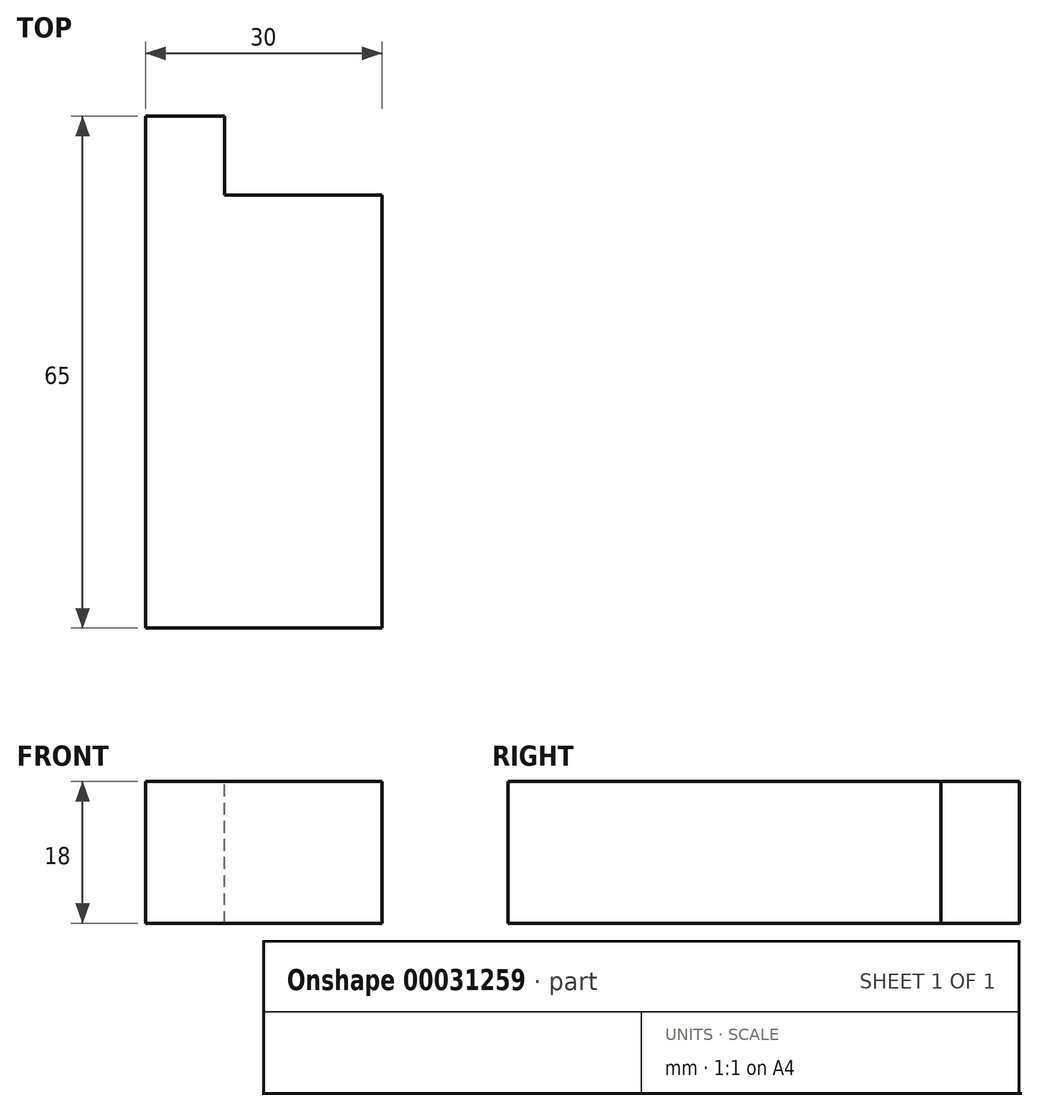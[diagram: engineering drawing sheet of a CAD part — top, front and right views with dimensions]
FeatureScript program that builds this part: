
annotation { "Feature Type Name" : "Feature", "Feature Type Description" : "" }
export const myFeature = defineFeature(function(context is Context, id is Id, definition is map)
    precondition{}
    {
        {
            var Q0;
            Q0=qCreatedBy(makeId("Top.planeOp"),FACE);
            var sketch = newSketch(context, id + "F0", { "sketchPlane" : qUnion([Q0])});
            skLineSegment(sketch, "E0.bottom", {"start": v(-15, 27.5) * mm, "end": v(15, 27.5) * mm});
            skLineSegment(sketch, "E0.top", {"start": v(-15, -27.5) * mm, "end": v(15, -27.5) * mm});
            skLineSegment(sketch, "E0.left", {"start": v(-15, 27.5) * mm, "end": v(-15, -27.5) * mm});
            skLineSegment(sketch, "E0.right", {"start": v(15, 27.5) * mm, "end": v(15, -27.5) * mm});
            skPoint(sketch, "E0.middle", {"position": v(0, 0) * mm});
            skSolve(sketch);
        }
        {
            var Q0;
            Q0 = qSketchRegion(id + "F0", true);
            extrude(context, id + "F1", {"entities" : qUnion([Q0]), "depth" : 18 * mm});
        }
        {
            var Q0;
            Q0=makeQuery(id+"F1.opExtrude","SWEPT_FACE",FACE,{"disambiguationData":[OSD([sQuery(id+"F0.wireOp",EDGE,"E0.bottom")])]});
            var sketch = newSketch(context, id + "F2", { "sketchPlane" : qUnion([Q0])});
            skLineSegment(sketch, "E1.bottom", {"start": v(15, 0) * mm, "end": v(5, 0) * mm});
            skLineSegment(sketch, "E1.top", {"start": v(15, 18) * mm, "end": v(5, 18) * mm});
            skLineSegment(sketch, "E1.left", {"start": v(15, 0) * mm, "end": v(15, 18) * mm});
            skLineSegment(sketch, "E1.right", {"start": v(5, 0) * mm, "end": v(5, 18) * mm});
            skSolve(sketch);
        }
        {
            var Q0;
            Q0 = qSketchRegion(id + "F2", true);
            extrude(context, id + "F3", {"entities" : qUnion([Q0]), "operationType" : NewBodyOperationType.ADD, "depth" : 10 * mm});
        }
    });
